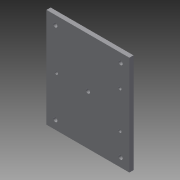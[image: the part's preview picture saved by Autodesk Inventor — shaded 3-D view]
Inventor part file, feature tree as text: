
AUTODESK INVENTOR PART (.ipt)
format: ipt  version: 2014 SP1 (Build 180222100, 222)  size: 97,280 bytes
history: native  units: in
note: dims shown in document units (in); Inventor stores cm internally (conversion verified against a paired STEP export)
features: extrude x1, sketch x1
ambient origin geometry x8: Origin, YZ Plane, XZ Plane, XY Plane, X Axis, Y Axis, Z Axis, Center Point
bodies: Solid1 (feature_tree)
feature tree (2):
  extrude  "Extrusion1"  Depth=6.0in
  sketch  "Sketch1"  dims[d0=5.0in d1=6.0in d2=0.75in d3=45.0deg d6=0.25in d7=0.25in d8=0.25in d9=0.25in d10=0.25in d11=1.9055in d12=1.9291in d13=1.1138in d14=1.1138in d15=0.189in d16=0.189in d17=0.189in d18=0.25in d19=0.0in]
